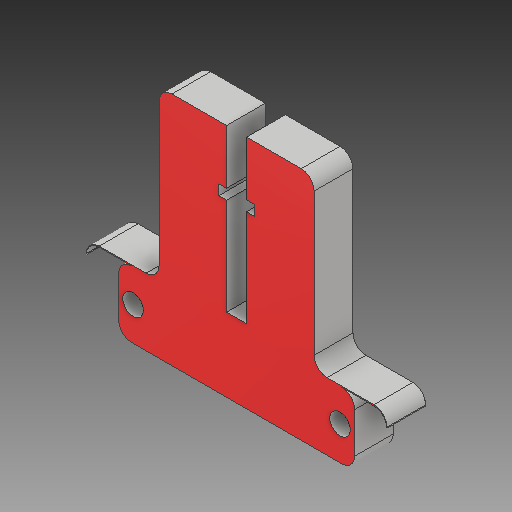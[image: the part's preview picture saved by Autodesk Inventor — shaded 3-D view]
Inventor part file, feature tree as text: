
AUTODESK INVENTOR PART (.ipt)
format: ipt  version: 2017 (Build 210142000, 142)  size: 177,664 bytes
history: native  units: mm
features: sketch x6, other x3
ambient origin geometry x8: Origin, YZ Plane, XZ Plane, XY Plane, X Axis, Y Axis, Z Axis, Center Point
bodies: Solid1 (feature_tree)
feature tree (9):
  other  "Hotend Slide Part 1.ipt"
  other  "Solid1::Hotend Slide Part 1.ipt"
  other  "TaggingFeature1"
  sketch  "Sketch1"  dims[d0=10.0mm]
  sketch  "Sketch2"
  sketch  "Sketch3"
  sketch  "Sketch4"
  sketch  "Sketch5"
  sketch  "Sketch6"
